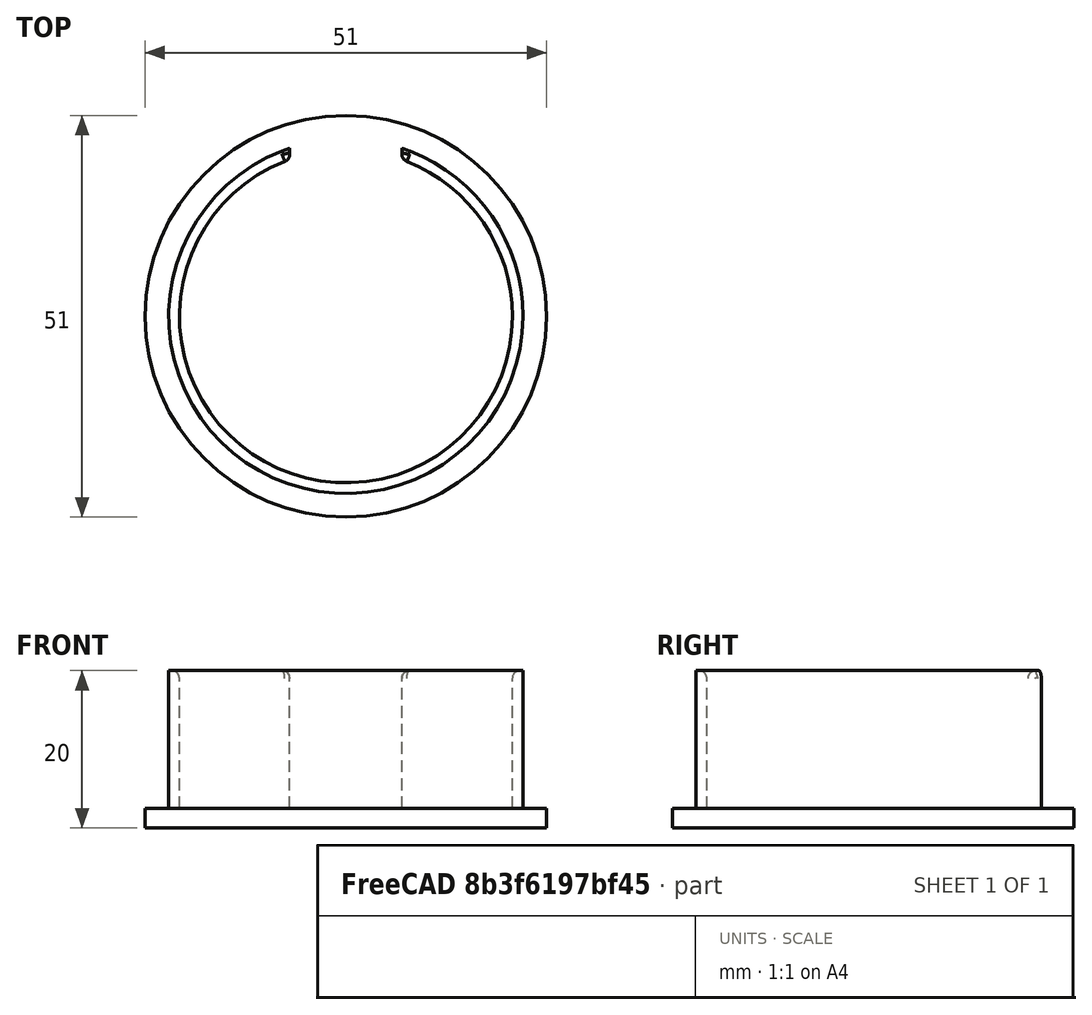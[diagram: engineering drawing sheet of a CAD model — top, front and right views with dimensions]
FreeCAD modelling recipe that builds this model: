
FCSTD DOCUMENT  (FreeCAD 0.17R13541 (Git))
Label: kinor-35-viewfinder-cap
License: All rights reserved
LicenseURL: http://en.wikipedia.org/wiki/All_rights_reserved
objects: Part::Cylinder×3, Part::Cut×2, Part::Fillet×2, Part::Box×1, Part::Fuse×1
note: 9 computed .brp shape members not serialized (recipe doc carries the construction recipe); baked Part::Feature solids carry a one-line shape summary decoded from their .brp

FEATURE [Part::Cylinder] Cylinder
  Angle = 360
  AttacherType = Attacher::AttachEngine3D
  Height = 2.5
  Radius = 25.5
FEATURE [Part::Cylinder] Cylinder001
  Angle = 360
  AttacherType = Attacher::AttachEngine3D
  Height = 20
  Radius = 22.5
FEATURE [Part::Cylinder] Cylinder002
  Angle = 360
  AttacherType = Attacher::AttachEngine3D
  Height = 30
  Placement = pos=(0,0,2.5) rot=(0,0,1;0rad)
  Radius = 21.15
FEATURE [Part::Cut] Cut
  Base = -> Cylinder001
  Tool = -> Cylinder002
FEATURE [Part::Box] Box  label="Cube"
  AttacherType = Attacher::AttachEngine3D
  Height = 20
  Length = 14.25
  Placement = pos=(-7.125,0,2.5) rot=(0,0,1;0rad)
  Width = 30
FEATURE [Part::Cut] Cut001
  Base = -> Cut
  Tool = -> Box
FEATURE [Part::Fillet] Fillet
  Base = -> Cut001
  Edges = 2 edges r=1: [Edge9,Edge10]
FEATURE [Part::Fillet] Fillet001
  Base = -> Fillet
  Edges = 4 edges r=1: [Edge1,Edge6,Edge8,Edge18]
FEATURE [Part::Fuse] Fusion  label="Viewfinder Cap"
  Base = -> Cylinder
  Tool = -> Fillet001
